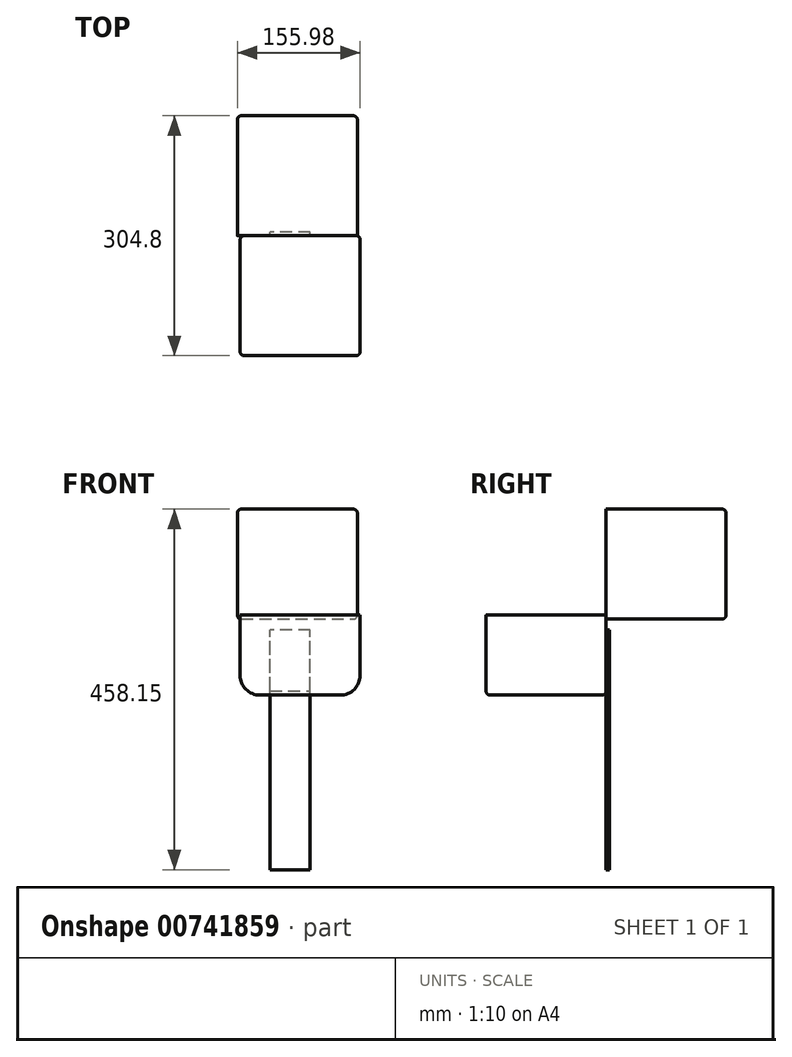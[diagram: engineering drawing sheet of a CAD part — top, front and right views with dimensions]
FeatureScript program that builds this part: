
annotation { "Feature Type Name" : "Feature", "Feature Type Description" : "" }
export const myFeature = defineFeature(function(context is Context, id is Id, definition is map)
    precondition{}
    {
        {
            var Q0;
            Q0=qCreatedBy(makeId("Front.planeOp"),FACE);
            var sketch = newSketch(context, id + "F0", { "sketchPlane" : qUnion([Q0])});
            skLineSegment(sketch, "E0.bottom", {"start": v(-58.6, 18.63) * mm, "end": v(93.8, 18.63) * mm});
            skLineSegment(sketch, "E0.top", {"start": v(-33.2, -82.97) * mm, "end": v(68.4, -82.97) * mm});
            skLineSegment(sketch, "E0.left", {"start": v(-58.6, 18.63) * mm, "end": v(-58.6, -57.57) * mm});
            skLineSegment(sketch, "E0.right", {"start": v(93.8, 18.63) * mm, "end": v(93.8, -57.57) * mm});
            skPoint(sketch, "E1.visualSharp", {"position": v(-58.6, -82.97) * mm});
            skArc(sketch, "E1.filletArc", {"start": v(-58.6, -57.57) * mm, "mid": v(-51.17, -75.53) * mm, "end": v(-33.2, -82.97) * mm});
            skPoint(sketch, "E2.visualSharp", {"position": v(93.8, -82.97) * mm});
            skArc(sketch, "E2.filletArc", {"start": v(68.4, -82.97) * mm, "mid": v(86.35, -75.53) * mm, "end": v(93.8, -57.57) * mm});
            skSolve(sketch);
        }
        {
            var Q0;
            Q0=makeQuery(id+"F0.imprint","IMPRINT",FACE,{"disambiguationData":[TD([[makeQuery(id+"F0.imprint","IMPRINT",EDGE,{"derivedFrom":sQuery(id+"F0.wireOp",EDGE,"E0.bottom")}),-1.0]])]});
            extrude(context, id + "F1", {"entities" : qUnion([Q0]), "depth" : 152.4 * mm, "offsetDistance" : 25.4 * mm});
        }
        {
            var Q0;
            Q0=makeQuery(id+"F1.opExtrude","CAP_EDGE",EDGE,{"disambiguationData":[OSD([sQuery(id+"F0.wireOp",EDGE,"E0.right")])],"isStart":false});
            var Q1;
            Q1=makeQuery(id+"F1.opExtrude","CAP_EDGE",EDGE,{"disambiguationData":[OSD([sQuery(id+"F0.wireOp",EDGE,"E0.right")])],"isStart":true});
            fillet(context, id + "F2", {"entities" : qUnion([Q0, Q1]), "radius" : 5.08 * mm, "tangentPropagation" : true, "allowEdgeOverflow" : false});
        }
        {
            var Q0;
            Q0=qCreatedBy(makeId("Front.planeOp"),FACE);
            var sketch = newSketch(context, id + "F3", { "sketchPlane" : qUnion([Q0])});
            skLineSegment(sketch, "E3.bottom", {"start": v(-62.2, 13.65) * mm, "end": v(90.2, 13.65) * mm});
            skLineSegment(sketch, "E3.top", {"start": v(-62.2, 153.35) * mm, "end": v(90.2, 153.35) * mm});
            skLineSegment(sketch, "E3.left", {"start": v(-62.2, 13.65) * mm, "end": v(-62.2, 153.35) * mm});
            skLineSegment(sketch, "E3.right", {"start": v(90.2, 13.65) * mm, "end": v(90.2, 153.35) * mm});
            skSolve(sketch);
        }
        {
            var Q0;
            Q0=makeQuery(id+"F3.imprint","IMPRINT",FACE,{"disambiguationData":[TD([[makeQuery(id+"F3.imprint","IMPRINT",EDGE,{"derivedFrom":sQuery(id+"F3.wireOp",EDGE,"E3.bottom")}),1.0]])]});
            extrude(context, id + "F4", {"entities" : qUnion([Q0]), "oppositeDirection" : true, "depth" : 152.4 * mm, "offsetDistance" : 25.4 * mm});
        }
        {
            var Q0;
            Q0=makeQuery(id+"F4.opExtrude","SWEPT_EDGE",EDGE,{"disambiguationData":[OSD([sQuery(id+"F3.wireOp",EDGE,"E3.top"),sQuery(id+"F3.wireOp",EDGE,"E3.right")])]});
            var Q1;
            Q1=makeQuery(id+"F4.opExtrude","SWEPT_EDGE",EDGE,{"disambiguationData":[OSD([sQuery(id+"F3.wireOp",EDGE,"E3.bottom"),sQuery(id+"F3.wireOp",EDGE,"E3.right")])]});
            var Q2;
            Q2=makeQuery(id+"F4.opExtrude","CAP_EDGE",EDGE,{"disambiguationData":[OSD([sQuery(id+"F3.wireOp",EDGE,"E3.right")])],"isStart":false});
            var Q3;
            Q3=makeQuery(id+"F4.opExtrude","SWEPT_EDGE",EDGE,{"disambiguationData":[OSD([sQuery(id+"F3.wireOp",EDGE,"E3.top"),sQuery(id+"F3.wireOp",EDGE,"E3.left")])]});
            var Q4;
            Q4=makeQuery(id+"F4.opExtrude","CAP_EDGE",EDGE,{"disambiguationData":[OSD([sQuery(id+"F3.wireOp",EDGE,"E3.top")])],"isStart":false});
            var Q5;
            Q5=makeQuery(id+"F4.opExtrude","SWEPT_EDGE",EDGE,{"disambiguationData":[OSD([sQuery(id+"F3.wireOp",EDGE,"E3.bottom"),sQuery(id+"F3.wireOp",EDGE,"E3.left")])]});
            var Q6;
            Q6=makeQuery(id+"F4.opExtrude","CAP_EDGE",EDGE,{"disambiguationData":[OSD([sQuery(id+"F3.wireOp",EDGE,"E3.left")])],"isStart":false});
            var Q7;
            Q7=makeQuery(id+"F4.opExtrude","CAP_EDGE",EDGE,{"disambiguationData":[OSD([sQuery(id+"F3.wireOp",EDGE,"E3.bottom")])],"isStart":false});
            fillet(context, id + "F5", {"entities" : qUnion([Q0, Q1, Q2, Q3, Q4, Q5, Q6, Q7]), "radius" : 5.08 * mm, "tangentPropagation" : true, "allowEdgeOverflow" : false});
        }
        {
            var Q0;
            Q0=qCreatedBy(makeId("Top.planeOp"),FACE);
            var sketch = newSketch(context, id + "F6", { "sketchPlane" : qUnion([Q0])});
            skLineSegment(sketch, "E4.bottom", {"start": v(30.25, 0) * mm, "end": v(-20.55, 0) * mm});
            skLineSegment(sketch, "E4.top", {"start": v(30.25, 4.48) * mm, "end": v(-20.55, 4.48) * mm});
            skLineSegment(sketch, "E4.left", {"start": v(30.25, 0) * mm, "end": v(30.25, 4.48) * mm});
            skLineSegment(sketch, "E4.right", {"start": v(-20.55, 0) * mm, "end": v(-20.55, 4.48) * mm});
            skSolve(sketch);
        }
        {
            var Q0;
            Q0=makeQuery(id+"F6.imprint","IMPRINT",FACE,{"disambiguationData":[TD([[makeQuery(id+"F6.imprint","IMPRINT",EDGE,{"derivedFrom":sQuery(id+"F6.wireOp",EDGE,"E4.bottom")}),-1.0]])]});
            extrude(context, id + "F7", {"entities" : qUnion([Q0]), "operationType" : NewBodyOperationType.ADD, "oppositeDirection" : true, "depth" : 304.8 * mm, "offsetDistance" : 25.4 * mm});
        }
    });
